# Revit family: EN_Bridge_basic
name_source: partatom
category: Allgemeines Modell
units: mm (PartAtom-declared; Revit-internal decimal feet)

## family parameters
Beim Laden mit Abzugskörper schneiden = Nein
Bemaßung runder Anschluss = Durchmesser verwenden
Beschriftungsausrichtung beibehalten = Nein
Gemeinsam genutzt = Nein
Kann Basisbauteil für Bewehrung sein = Nein
Raumberechnungspunkt = Nein
Teiletyp = Normal

## types (5) — shared parameters
Ausschreiben.de = https://ausschreiben.de
Bauelement = Entwässerungsrinnen Oberflächenwasser
Beschreibung = Universal Entwässerungssystem aus Polymerbeton für Belastungsklassen bis D400
Construction drainage = Hohlbordrinne für Brücken
Hersteller = MEA Bautechnik GmbH Geschäftsbereich MEA Water Management
Hersteller und Typ - Ausschreibender gleichwertig = wie MEA Bautechnik GmbH, Modell MEA…...
IfcDescription = Universal Entwässerungssystem aus Polymerbeton für Belastungsklassen bis D400
IfcExportAs = IfcWasteTerminalType
IfcExportType = USERDEFINED
MEA planning assistance = https://www.mea-group.com
Material fundation = -
Outlet diameter = 160 mm
STLB Bau Mustervorlage = https://www.stlb-bau-online.de
Stutzendurchmesser_innen = 156 mm  [stored 0.511811 ft]
Type drainage component = Typ M
URL = https://www.mea-group.com
component drainage = Entwässerungsrinne
execution documents = gemäß Zeichnung und Einzelbeschreibung
guid = cf6c1bd8-9bf4-4563-8c57-07955e2378ac
installation technology = siehe Einbauanleitung
product website = https://www.mea-group.com
technical product information = https://www.mea-group.com
zero-valued in all types: Vorgabe-Ansicht

## per-type parameters (varying)
| type | Channel height | Channel width | Deckelexbeginn | Deckelöffnung | Einbauversatz | Halbe Rinnenbreite | Installation height | Kopfstärke | MEA-Artikelnummer | Modell | Radius head | Rev_Breits | Rev_Position | Revision length | Revision width | Stutzenanfang | Stutzenlänge | clear width mm drainage | gratin depth | height square | wall thickness |
| MEAKERB Bridge 160/125 | 200 mm | 220 mm | 130 mm  [stored 0.426509 ft] | 85 mm  [stored 0.278871 ft] | 75 mm | 110 mm  [stored 0.360892 ft] | 125 mm  [stored 0.410105 ft] | 40 mm  [stored 0.131234 ft] | 010152170 | MEAKERB BRIDGE 160/125 | 60 mm  [stored 0.19685 ft] | 63 mm | 150 mm | 300 mm | 126 mm | -75 mm | -225 mm  [stored -0.738189 ft] | 160 | 25 mm  [stored 0.082021 ft] | 135 mm  [stored 0.442913 ft] | 30 mm  [stored 0.0984252 ft] |
| MEAKERB Bridge 160/150 | 200 mm | 220 mm | 155 mm  [stored 0.50853 ft] | 110 mm  [stored 0.360892 ft] | 50 mm  [stored 0.164042 ft] | 110 mm  [stored 0.360892 ft] | 150 mm | 40 mm  [stored 0.131234 ft] | 010152174 | MEAKERB BRIDGE 160/150 | 60 mm  [stored 0.19685 ft] | 63 mm | 150 mm | 300 mm | 126 mm | -50 mm  [stored -0.164042 ft] | -200 mm  [stored -0.656168 ft] | 160 | 25 mm  [stored 0.082021 ft] | 135 mm  [stored 0.442913 ft] | 30 mm  [stored 0.0984252 ft] |
| MEAKERB Bridge 200/75 | 155 mm  [stored 0.50853 ft] | 280 mm | 80 mm  [stored 0.262467 ft] | 26 mm | 80 mm  [stored 0.262467 ft] | 140 mm  [stored 0.459318 ft] | 75 mm | 49 mm | 010152205 | MEAKERB BRIDGE 200/75 | 10 mm  [stored 0.0328084 ft] | 66 mm  [stored 0.216535 ft] | 142 mm | 283 mm | 132 mm  [stored 0.433071 ft] | -80 mm  [stored -0.262467 ft] | -230 mm  [stored -0.754593 ft] | 200 | 23 mm  [stored 0.0754593 ft] | 83 mm  [stored 0.27231 ft] | 40 mm  [stored 0.131234 ft] |
| MEAKERB Bridge 160/125 OPA | 200 mm | 220 mm | 130 mm  [stored 0.426509 ft] | 85 mm  [stored 0.278871 ft] | 75 mm | 110 mm  [stored 0.360892 ft] | 125 mm  [stored 0.410105 ft] | 40 mm  [stored 0.131234 ft] | 010152184 | MEAKERB BRIDGE 160/125 OPA | 60 mm  [stored 0.19685 ft] | 63 mm | 150 mm | 300 mm | 126 mm | -75 mm | -225 mm  [stored -0.738189 ft] | 160 | 25 mm  [stored 0.082021 ft] | 135 mm  [stored 0.442913 ft] | 30 mm  [stored 0.0984252 ft] |
| MEAKERB Bridge 200/75 OPA | 175 mm | 280 mm | 80 mm  [stored 0.262467 ft] | 24 mm | 100 mm  [stored 0.328084 ft] | 140 mm  [stored 0.459318 ft] | 75 mm | 51 mm | 010152212 | MEAKERB BRIDGE 200/75 OPA | 20 mm  [stored 0.0656168 ft] | 66 mm  [stored 0.216535 ft] | 142 mm | 283 mm | 132 mm  [stored 0.433071 ft] | -100 mm  [stored -0.328084 ft] | -250 mm  [stored -0.82021 ft] | 200 | 23 mm  [stored 0.0754593 ft] | 101 mm  [stored 0.331365 ft] | 40 mm  [stored 0.131234 ft] |

note: [stored X ft] marks values corroborated as IEEE doubles in the binary element streams (Revit-internal decimal feet)
